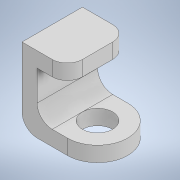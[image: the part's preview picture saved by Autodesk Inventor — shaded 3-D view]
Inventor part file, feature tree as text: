
AUTODESK INVENTOR PART (.ipt)
format: ipt  version: 2020 (Build 240168000, 168)  size: 129,536 bytes
history: native  units: mm
features: fillet x2, sketch x2, extrude x1, hole x1
ambient origin geometry x8: Origin, YZ Plane, XZ Plane, XY Plane, X Axis, Y Axis, Z Axis, Center Point
bodies: Solid1 (feature_tree)
feature tree (6):
  extrude  "Extrusion1"  Depth=10.0mm
  fillet  "Fillet1"  Radius=10.0mm
  fillet  "Fillet2"  Radius=10.0mm
  hole  "Hole1"  [1 undecoded]
  sketch  "Sketch1"  dims[d0=30.0mm d2=50.0mm d3=10.0mm d5=10.0mm]
  sketch  "Sketch2"  dims[d6=10.0mm d7=40.0mm d8=0.0mm d9=20.0mm d10=10.0mm d11=20.0mm d12=38.1mm d13=3.023mm d14=2.0mm d15=14.3117mm d16=8.0mm d17=20.594885mm]
note: 1 required parameter value undecoded (feature->parameter linkage not recoverable at this tier; creation-order binding heuristic only, values carry confidence <= 0.55)
